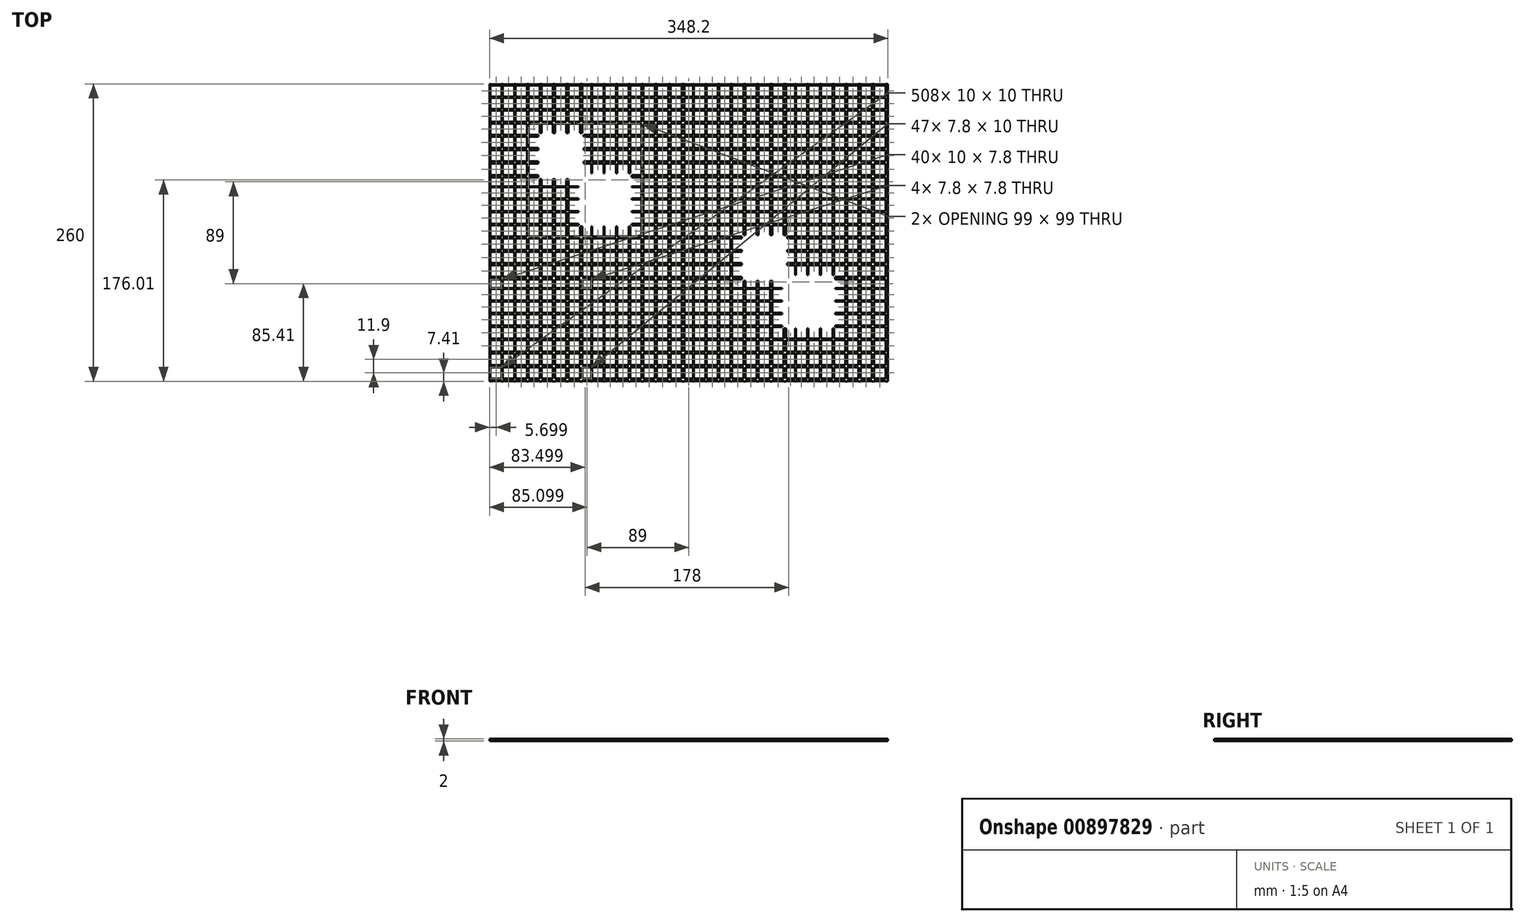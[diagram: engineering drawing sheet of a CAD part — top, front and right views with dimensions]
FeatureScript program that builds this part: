
annotation { "Feature Type Name" : "Feature", "Feature Type Description" : "" }
export const myFeature = defineFeature(function(context is Context, id is Id, definition is map)
    precondition{}
    {
        {
            var Q0;
            Q0=qCreatedBy(makeId("Top.planeOp"),FACE);
            var sketch = newSketch(context, id + "F0", { "sketchPlane" : qUnion([Q0])});
            skLineSegment(sketch, "E0.bottom", {"start": v(-169.44, 136.35) * mm, "end": v(-168.74, 136.35) * mm});
            skLineSegment(sketch, "E0.top", {"start": v(-169.44, -123.65) * mm, "end": v(-168.74, -123.65) * mm});
            skLineSegment(sketch, "E0.left", {"start": v(-169.44, 136.35) * mm, "end": v(-169.44, -123.65) * mm});
            skLineSegment(sketch, "E0.right", {"start": v(-168.74, 136.35) * mm, "end": v(-168.74, -123.65) * mm});
            skLineSegment(sketch, "E1.bottom", {"start": v(-158.74, 136.35) * mm, "end": v(-157.84, 136.35) * mm});
            skLineSegment(sketch, "E1.top", {"start": v(-158.74, -123.65) * mm, "end": v(-157.84, -123.65) * mm});
            skLineSegment(sketch, "E1.left", {"start": v(-158.74, 136.35) * mm, "end": v(-158.74, -123.65) * mm});
            skLineSegment(sketch, "E1.right", {"start": v(-157.84, 136.35) * mm, "end": v(-157.84, -123.65) * mm});
            skLineSegment(sketch, "E2.bottom", {"start": v(-147.84, 136.35) * mm, "end": v(-146.74, 136.35) * mm});
            skLineSegment(sketch, "E2.top", {"start": v(-147.84, -123.65) * mm, "end": v(-146.74, -123.65) * mm});
            skLineSegment(sketch, "E2.left", {"start": v(-147.84, 136.35) * mm, "end": v(-147.84, -123.65) * mm});
            skLineSegment(sketch, "E2.right", {"start": v(-146.74, 136.35) * mm, "end": v(-146.74, -123.65) * mm});
            skLineSegment(sketch, "E3.bottom", {"start": v(-136.74, 136.35) * mm, "end": v(-135.44, 136.35) * mm});
            skLineSegment(sketch, "E3.top", {"start": v(-136.74, -123.65) * mm, "end": v(-135.44, -123.65) * mm});
            skLineSegment(sketch, "E3.left", {"start": v(-136.74, 136.35) * mm, "end": v(-136.74, -123.65) * mm});
            skLineSegment(sketch, "E3.right", {"start": v(-135.44, 136.35) * mm, "end": v(-135.44, -123.65) * mm});
            skLineSegment(sketch, "E4.bottom", {"start": v(-125.44, 136.35) * mm, "end": v(-123.94, 136.35) * mm});
            skLineSegment(sketch, "E4.top", {"start": v(-125.44, -123.65) * mm, "end": v(-123.94, -123.65) * mm});
            skLineSegment(sketch, "E4.left", {"start": v(-125.44, 136.35) * mm, "end": v(-125.44, -123.65) * mm});
            skLineSegment(sketch, "E4.right", {"start": v(-123.94, 136.35) * mm, "end": v(-123.94, -123.65) * mm});
            skLineSegment(sketch, "E5.bottom", {"start": v(-113.94, 136.35) * mm, "end": v(-112.24, 136.35) * mm});
            skLineSegment(sketch, "E5.top", {"start": v(-113.94, -123.65) * mm, "end": v(-112.24, -123.65) * mm});
            skLineSegment(sketch, "E5.left", {"start": v(-113.94, 136.35) * mm, "end": v(-113.94, -123.65) * mm});
            skLineSegment(sketch, "E5.right", {"start": v(-112.24, 136.35) * mm, "end": v(-112.24, -123.65) * mm});
            skLineSegment(sketch, "E6.bottom", {"start": v(-102.24, 136.35) * mm, "end": v(-100.34, 136.35) * mm});
            skLineSegment(sketch, "E6.top", {"start": v(-102.24, -123.65) * mm, "end": v(-100.34, -123.65) * mm});
            skLineSegment(sketch, "E6.left", {"start": v(-102.24, 136.35) * mm, "end": v(-102.24, -123.65) * mm});
            skLineSegment(sketch, "E6.right", {"start": v(-100.34, 136.35) * mm, "end": v(-100.34, -123.65) * mm});
            skLineSegment(sketch, "E7.bottom", {"start": v(-90.34, 136.35) * mm, "end": v(-88.24, 136.35) * mm});
            skLineSegment(sketch, "E7.top", {"start": v(-90.34, -123.65) * mm, "end": v(-88.24, -123.65) * mm});
            skLineSegment(sketch, "E7.left", {"start": v(-90.34, 136.35) * mm, "end": v(-90.34, -123.65) * mm});
            skLineSegment(sketch, "E7.right", {"start": v(-88.24, 136.35) * mm, "end": v(-88.24, -123.65) * mm});
            skLineSegment(sketch, "E8.1.0.0", {"start": v(-69.74, 136.35) * mm, "end": v(-69.74, -123.65) * mm});
            skLineSegment(sketch, "E8.1.0.1", {"start": v(-13.24, 136.35) * mm, "end": v(-13.24, -123.65) * mm});
            skLineSegment(sketch, "E8.1.0.2", {"start": v(-58.84, 136.35) * mm, "end": v(-58.84, -123.65) * mm});
            skLineSegment(sketch, "E8.1.0.3", {"start": v(-79.74, 136.35) * mm, "end": v(-79.74, -123.65) * mm});
            skLineSegment(sketch, "E8.1.0.4", {"start": v(-68.84, 136.35) * mm, "end": v(-68.84, -123.65) * mm});
            skLineSegment(sketch, "E8.1.0.5", {"start": v(-1.34, 136.35) * mm, "end": v(-1.34, -123.65) * mm});
            skLineSegment(sketch, "E8.1.0.6", {"start": v(-24.94, 136.35) * mm, "end": v(-24.94, -123.65) * mm});
            skLineSegment(sketch, "E8.1.0.7", {"start": v(-36.44, 136.35) * mm, "end": v(-36.44, -123.65) * mm});
            skLineSegment(sketch, "E8.1.0.8", {"start": v(-80.44, 136.35) * mm, "end": v(-80.44, -123.65) * mm});
            skLineSegment(sketch, "E8.1.0.9", {"start": v(-47.74, 136.35) * mm, "end": v(-47.74, -123.65) * mm});
            skLineSegment(sketch, "E8.1.0.10", {"start": v(-11.34, 136.35) * mm, "end": v(-11.34, -123.65) * mm});
            skLineSegment(sketch, "E8.1.0.11", {"start": v(-34.94, 136.35) * mm, "end": v(-34.94, -123.65) * mm});
            skLineSegment(sketch, "E8.1.0.12", {"start": v(0.76, 136.35) * mm, "end": v(0.76, -123.65) * mm});
            skLineSegment(sketch, "E8.1.0.13", {"start": v(-23.24, 136.35) * mm, "end": v(-23.24, -123.65) * mm});
            skLineSegment(sketch, "E8.1.0.14", {"start": v(-57.74, 136.35) * mm, "end": v(-57.74, -123.65) * mm});
            skLineSegment(sketch, "E8.1.0.15", {"start": v(-46.44, 136.35) * mm, "end": v(-46.44, -123.65) * mm});
            skLineSegment(sketch, "E8.1.0.16", {"start": v(-69.74, -123.65) * mm, "end": v(-68.84, -123.65) * mm});
            skLineSegment(sketch, "E8.1.0.17", {"start": v(-58.84, 136.35) * mm, "end": v(-57.74, 136.35) * mm});
            skLineSegment(sketch, "E8.1.0.18", {"start": v(-13.24, -123.65) * mm, "end": v(-11.34, -123.65) * mm});
            skLineSegment(sketch, "E8.1.0.19", {"start": v(-36.44, -123.65) * mm, "end": v(-34.94, -123.65) * mm});
            skLineSegment(sketch, "E8.1.0.20", {"start": v(-1.34, 136.35) * mm, "end": v(0.76, 136.35) * mm});
            skLineSegment(sketch, "E8.1.0.21", {"start": v(-69.74, 136.35) * mm, "end": v(-68.84, 136.35) * mm});
            skLineSegment(sketch, "E8.1.0.22", {"start": v(-80.44, -123.65) * mm, "end": v(-79.74, -123.65) * mm});
            skLineSegment(sketch, "E8.1.0.23", {"start": v(-36.44, 136.35) * mm, "end": v(-34.94, 136.35) * mm});
            skLineSegment(sketch, "E8.1.0.24", {"start": v(-80.44, 136.35) * mm, "end": v(-79.74, 136.35) * mm});
            skLineSegment(sketch, "E8.1.0.25", {"start": v(-24.94, 136.35) * mm, "end": v(-23.24, 136.35) * mm});
            skLineSegment(sketch, "E8.1.0.26", {"start": v(-58.84, -123.65) * mm, "end": v(-57.74, -123.65) * mm});
            skLineSegment(sketch, "E8.1.0.27", {"start": v(-1.34, -123.65) * mm, "end": v(0.76, -123.65) * mm});
            skLineSegment(sketch, "E8.1.0.28", {"start": v(-13.24, 136.35) * mm, "end": v(-11.34, 136.35) * mm});
            skLineSegment(sketch, "E8.1.0.29", {"start": v(-24.94, -123.65) * mm, "end": v(-23.24, -123.65) * mm});
            skLineSegment(sketch, "E8.1.0.30", {"start": v(-47.74, 136.35) * mm, "end": v(-46.44, 136.35) * mm});
            skLineSegment(sketch, "E8.1.0.31", {"start": v(-47.74, -123.65) * mm, "end": v(-46.44, -123.65) * mm});
            skLineSegment(sketch, "E8.2.0.0", {"start": v(19.26, 136.35) * mm, "end": v(19.26, -123.65) * mm});
            skLineSegment(sketch, "E8.2.0.1", {"start": v(75.76, 136.35) * mm, "end": v(75.76, -123.65) * mm});
            skLineSegment(sketch, "E8.2.0.2", {"start": v(30.16, 136.35) * mm, "end": v(30.16, -123.65) * mm});
            skLineSegment(sketch, "E8.2.0.3", {"start": v(9.26, 136.35) * mm, "end": v(9.26, -123.65) * mm});
            skLineSegment(sketch, "E8.2.0.4", {"start": v(20.16, 136.35) * mm, "end": v(20.16, -123.65) * mm});
            skLineSegment(sketch, "E8.2.0.5", {"start": v(87.66, 136.35) * mm, "end": v(87.66, -123.65) * mm});
            skLineSegment(sketch, "E8.2.0.6", {"start": v(64.06, 136.35) * mm, "end": v(64.06, -123.65) * mm});
            skLineSegment(sketch, "E8.2.0.7", {"start": v(52.56, 136.35) * mm, "end": v(52.56, -123.65) * mm});
            skLineSegment(sketch, "E8.2.0.8", {"start": v(8.56, 136.35) * mm, "end": v(8.56, -123.65) * mm});
            skLineSegment(sketch, "E8.2.0.9", {"start": v(41.26, 136.35) * mm, "end": v(41.26, -123.65) * mm});
            skLineSegment(sketch, "E8.2.0.10", {"start": v(77.66, 136.35) * mm, "end": v(77.66, -123.65) * mm});
            skLineSegment(sketch, "E8.2.0.11", {"start": v(54.06, 136.35) * mm, "end": v(54.06, -123.65) * mm});
            skLineSegment(sketch, "E8.2.0.12", {"start": v(89.76, 136.35) * mm, "end": v(89.76, -123.65) * mm});
            skLineSegment(sketch, "E8.2.0.13", {"start": v(65.76, 136.35) * mm, "end": v(65.76, -123.65) * mm});
            skLineSegment(sketch, "E8.2.0.14", {"start": v(31.26, 136.35) * mm, "end": v(31.26, -123.65) * mm});
            skLineSegment(sketch, "E8.2.0.15", {"start": v(42.56, 136.35) * mm, "end": v(42.56, -123.65) * mm});
            skLineSegment(sketch, "E8.2.0.16", {"start": v(19.26, -123.65) * mm, "end": v(20.16, -123.65) * mm});
            skLineSegment(sketch, "E8.2.0.17", {"start": v(30.16, 136.35) * mm, "end": v(31.26, 136.35) * mm});
            skLineSegment(sketch, "E8.2.0.18", {"start": v(75.76, -123.65) * mm, "end": v(77.66, -123.65) * mm});
            skLineSegment(sketch, "E8.2.0.19", {"start": v(52.56, -123.65) * mm, "end": v(54.06, -123.65) * mm});
            skLineSegment(sketch, "E8.2.0.20", {"start": v(87.66, 136.35) * mm, "end": v(89.76, 136.35) * mm});
            skLineSegment(sketch, "E8.2.0.21", {"start": v(19.26, 136.35) * mm, "end": v(20.16, 136.35) * mm});
            skLineSegment(sketch, "E8.2.0.22", {"start": v(8.56, -123.65) * mm, "end": v(9.26, -123.65) * mm});
            skLineSegment(sketch, "E8.2.0.23", {"start": v(52.56, 136.35) * mm, "end": v(54.06, 136.35) * mm});
            skLineSegment(sketch, "E8.2.0.24", {"start": v(8.56, 136.35) * mm, "end": v(9.26, 136.35) * mm});
            skLineSegment(sketch, "E8.2.0.25", {"start": v(64.06, 136.35) * mm, "end": v(65.76, 136.35) * mm});
            skLineSegment(sketch, "E8.2.0.26", {"start": v(30.16, -123.65) * mm, "end": v(31.26, -123.65) * mm});
            skLineSegment(sketch, "E8.2.0.27", {"start": v(87.66, -123.65) * mm, "end": v(89.76, -123.65) * mm});
            skLineSegment(sketch, "E8.2.0.28", {"start": v(75.76, 136.35) * mm, "end": v(77.66, 136.35) * mm});
            skLineSegment(sketch, "E8.2.0.29", {"start": v(64.06, -123.65) * mm, "end": v(65.76, -123.65) * mm});
            skLineSegment(sketch, "E8.2.0.30", {"start": v(41.26, 136.35) * mm, "end": v(42.56, 136.35) * mm});
            skLineSegment(sketch, "E8.2.0.31", {"start": v(41.26, -123.65) * mm, "end": v(42.56, -123.65) * mm});
            skLineSegment(sketch, "E8.direction1", {"start": v(-169.44, -123.65) * mm, "end": v(-80.44, -123.65) * mm, "construction": true});
            skLineSegment(sketch, "E9.0.3.0", {"start": v(108.26, 136.35) * mm, "end": v(108.26, -123.65) * mm});
            skLineSegment(sketch, "E9.3.3.0", {"start": v(164.76, 136.35) * mm, "end": v(164.76, -123.65) * mm});
            skLineSegment(sketch, "E9.6.3.0", {"start": v(119.16, 136.35) * mm, "end": v(119.16, -123.65) * mm});
            skLineSegment(sketch, "E9.9.3.0", {"start": v(98.26, 136.35) * mm, "end": v(98.26, -123.65) * mm});
            skLineSegment(sketch, "E9.12.3.0", {"start": v(109.16, 136.35) * mm, "end": v(109.16, -123.65) * mm});
            skLineSegment(sketch, "E9.15.3.0", {"start": v(176.66, 136.35) * mm, "end": v(176.66, -123.65) * mm});
            skLineSegment(sketch, "E9.18.3.0", {"start": v(153.06, 136.35) * mm, "end": v(153.06, -123.65) * mm});
            skLineSegment(sketch, "E9.21.3.0", {"start": v(141.56, 136.35) * mm, "end": v(141.56, -123.65) * mm});
            skLineSegment(sketch, "E9.24.3.0", {"start": v(97.56, 136.35) * mm, "end": v(97.56, -123.65) * mm});
            skLineSegment(sketch, "E9.27.3.0", {"start": v(130.26, 136.35) * mm, "end": v(130.26, -123.65) * mm});
            skLineSegment(sketch, "E9.30.3.0", {"start": v(166.66, 136.35) * mm, "end": v(166.66, -123.65) * mm});
            skLineSegment(sketch, "E9.33.3.0", {"start": v(143.06, 136.35) * mm, "end": v(143.06, -123.65) * mm});
            skLineSegment(sketch, "E9.36.3.0", {"start": v(178.76, 136.35) * mm, "end": v(178.76, -123.65) * mm});
            skLineSegment(sketch, "E9.39.3.0", {"start": v(154.76, 136.35) * mm, "end": v(154.76, -123.65) * mm});
            skLineSegment(sketch, "E9.42.3.0", {"start": v(120.26, 136.35) * mm, "end": v(120.26, -123.65) * mm});
            skLineSegment(sketch, "E9.45.3.0", {"start": v(131.56, 136.35) * mm, "end": v(131.56, -123.65) * mm});
            skLineSegment(sketch, "E9.48.3.0", {"start": v(108.26, -123.65) * mm, "end": v(109.16, -123.65) * mm});
            skLineSegment(sketch, "E9.51.3.0", {"start": v(119.16, 136.35) * mm, "end": v(120.26, 136.35) * mm});
            skLineSegment(sketch, "E9.54.3.0", {"start": v(164.76, -123.65) * mm, "end": v(166.66, -123.65) * mm});
            skLineSegment(sketch, "E9.57.3.0", {"start": v(141.56, -123.65) * mm, "end": v(143.06, -123.65) * mm});
            skLineSegment(sketch, "E9.60.3.0", {"start": v(176.66, 136.35) * mm, "end": v(178.76, 136.35) * mm});
            skLineSegment(sketch, "E9.63.3.0", {"start": v(108.26, 136.35) * mm, "end": v(109.16, 136.35) * mm});
            skLineSegment(sketch, "E9.66.3.0", {"start": v(97.56, -123.65) * mm, "end": v(98.26, -123.65) * mm});
            skLineSegment(sketch, "E9.69.3.0", {"start": v(141.56, 136.35) * mm, "end": v(143.06, 136.35) * mm});
            skLineSegment(sketch, "E9.72.3.0", {"start": v(97.56, 136.35) * mm, "end": v(98.26, 136.35) * mm});
            skLineSegment(sketch, "E9.75.3.0", {"start": v(153.06, 136.35) * mm, "end": v(154.76, 136.35) * mm});
            skLineSegment(sketch, "E9.78.3.0", {"start": v(119.16, -123.65) * mm, "end": v(120.26, -123.65) * mm});
            skLineSegment(sketch, "E9.81.3.0", {"start": v(176.66, -123.65) * mm, "end": v(178.76, -123.65) * mm});
            skLineSegment(sketch, "E9.84.3.0", {"start": v(164.76, 136.35) * mm, "end": v(166.66, 136.35) * mm});
            skLineSegment(sketch, "E9.87.3.0", {"start": v(153.06, -123.65) * mm, "end": v(154.76, -123.65) * mm});
            skLineSegment(sketch, "E9.90.3.0", {"start": v(130.26, 136.35) * mm, "end": v(131.56, 136.35) * mm});
            skLineSegment(sketch, "E9.93.3.0", {"start": v(130.26, -123.65) * mm, "end": v(131.56, -123.65) * mm});
            skSolve(sketch);
        }
        {
            var Q0;
            Q0 = qSketchRegion(id + "F0", true);
            extrude(context, id + "F1", {"entities" : qUnion([Q0]), "depth" : 2 * mm, "offsetDistance" : 25 * mm});
        }
        {
            var Q0;
            Q0=qCreatedBy(makeId("Top.planeOp"),FACE);
            var sketch = newSketch(context, id + "F2", { "sketchPlane" : qUnion([Q0])});
            skLineSegment(sketch, "E10.bottom", {"start": v(178.3, 135.86) * mm, "end": v(178.3, 135.16) * mm});
            skLineSegment(sketch, "E10.top", {"start": v(-169.1, 135.86) * mm, "end": v(-169.1, 135.16) * mm});
            skLineSegment(sketch, "E10.left", {"start": v(178.3, 135.86) * mm, "end": v(-169.1, 135.86) * mm});
            skLineSegment(sketch, "E10.right", {"start": v(178.3, 135.16) * mm, "end": v(-169.1, 135.16) * mm});
            skLineSegment(sketch, "E11.bottom", {"start": v(178.3, 125.16) * mm, "end": v(178.3, 124.26) * mm});
            skLineSegment(sketch, "E11.top", {"start": v(-169.1, 125.16) * mm, "end": v(-169.1, 124.26) * mm});
            skLineSegment(sketch, "E11.left", {"start": v(178.3, 125.16) * mm, "end": v(-169.1, 125.16) * mm});
            skLineSegment(sketch, "E11.right", {"start": v(178.3, 124.26) * mm, "end": v(-169.1, 124.26) * mm});
            skLineSegment(sketch, "E12.bottom", {"start": v(178.3, 114.26) * mm, "end": v(178.3, 113.16) * mm});
            skLineSegment(sketch, "E12.top", {"start": v(-169.1, 114.26) * mm, "end": v(-169.1, 113.16) * mm});
            skLineSegment(sketch, "E12.left", {"start": v(178.3, 114.26) * mm, "end": v(-169.1, 114.26) * mm});
            skLineSegment(sketch, "E12.right", {"start": v(178.3, 113.16) * mm, "end": v(-169.1, 113.16) * mm});
            skLineSegment(sketch, "E13.bottom", {"start": v(178.3, 103.16) * mm, "end": v(178.3, 101.86) * mm});
            skLineSegment(sketch, "E13.top", {"start": v(-169.1, 103.16) * mm, "end": v(-169.1, 101.86) * mm});
            skLineSegment(sketch, "E13.left", {"start": v(178.3, 103.16) * mm, "end": v(-169.1, 103.16) * mm});
            skLineSegment(sketch, "E13.right", {"start": v(178.3, 101.86) * mm, "end": v(-169.1, 101.86) * mm});
            skLineSegment(sketch, "E14.bottom", {"start": v(178.3, 91.86) * mm, "end": v(178.3, 90.36) * mm});
            skLineSegment(sketch, "E14.top", {"start": v(-169.1, 91.86) * mm, "end": v(-169.1, 90.36) * mm});
            skLineSegment(sketch, "E14.left", {"start": v(178.3, 91.86) * mm, "end": v(-169.1, 91.86) * mm});
            skLineSegment(sketch, "E14.right", {"start": v(178.3, 90.36) * mm, "end": v(-169.1, 90.36) * mm});
            skLineSegment(sketch, "E15.bottom", {"start": v(178.3, 80.36) * mm, "end": v(178.3, 78.66) * mm});
            skLineSegment(sketch, "E15.top", {"start": v(-169.1, 80.36) * mm, "end": v(-169.1, 78.66) * mm});
            skLineSegment(sketch, "E15.left", {"start": v(178.3, 80.36) * mm, "end": v(-169.1, 80.36) * mm});
            skLineSegment(sketch, "E15.right", {"start": v(178.3, 78.66) * mm, "end": v(-169.1, 78.66) * mm});
            skLineSegment(sketch, "E16.bottom", {"start": v(178.3, 68.66) * mm, "end": v(178.3, 66.76) * mm});
            skLineSegment(sketch, "E16.top", {"start": v(-169.1, 68.66) * mm, "end": v(-169.1, 66.76) * mm});
            skLineSegment(sketch, "E16.left", {"start": v(178.3, 68.66) * mm, "end": v(-169.1, 68.66) * mm});
            skLineSegment(sketch, "E16.right", {"start": v(178.3, 66.76) * mm, "end": v(-169.1, 66.76) * mm});
            skLineSegment(sketch, "E17.bottom", {"start": v(178.3, 56.76) * mm, "end": v(178.3, 54.66) * mm});
            skLineSegment(sketch, "E17.top", {"start": v(-169.1, 56.76) * mm, "end": v(-169.1, 54.66) * mm});
            skLineSegment(sketch, "E17.left", {"start": v(178.3, 56.76) * mm, "end": v(-169.1, 56.76) * mm});
            skLineSegment(sketch, "E17.right", {"start": v(178.3, 54.66) * mm, "end": v(-169.1, 54.66) * mm});
            skLineSegment(sketch, "E18.1.0.0", {"start": v(178.3, 36.16) * mm, "end": v(-169.1, 36.16) * mm});
            skLineSegment(sketch, "E18.1.0.1", {"start": v(178.3, -20.34) * mm, "end": v(-169.1, -20.34) * mm});
            skLineSegment(sketch, "E18.1.0.2", {"start": v(178.3, 25.26) * mm, "end": v(-169.1, 25.26) * mm});
            skLineSegment(sketch, "E18.1.0.3", {"start": v(178.3, 46.16) * mm, "end": v(-169.1, 46.16) * mm});
            skLineSegment(sketch, "E18.1.0.4", {"start": v(178.3, 35.26) * mm, "end": v(-169.1, 35.26) * mm});
            skLineSegment(sketch, "E18.1.0.5", {"start": v(178.3, -32.24) * mm, "end": v(-169.1, -32.24) * mm});
            skLineSegment(sketch, "E18.1.0.6", {"start": v(178.3, -8.64) * mm, "end": v(-169.1, -8.64) * mm});
            skLineSegment(sketch, "E18.1.0.7", {"start": v(178.3, 2.86) * mm, "end": v(-169.1, 2.86) * mm});
            skLineSegment(sketch, "E18.1.0.8", {"start": v(178.3, 46.86) * mm, "end": v(-169.1, 46.86) * mm});
            skLineSegment(sketch, "E18.1.0.9", {"start": v(178.3, 14.16) * mm, "end": v(-169.1, 14.16) * mm});
            skLineSegment(sketch, "E18.1.0.10", {"start": v(178.3, -22.24) * mm, "end": v(-169.1, -22.24) * mm});
            skLineSegment(sketch, "E18.1.0.11", {"start": v(178.3, 1.36) * mm, "end": v(-169.1, 1.36) * mm});
            skLineSegment(sketch, "E18.1.0.12", {"start": v(178.3, -34.34) * mm, "end": v(-169.1, -34.34) * mm});
            skLineSegment(sketch, "E18.1.0.13", {"start": v(178.3, -10.34) * mm, "end": v(-169.1, -10.34) * mm});
            skLineSegment(sketch, "E18.1.0.14", {"start": v(178.3, 24.16) * mm, "end": v(-169.1, 24.16) * mm});
            skLineSegment(sketch, "E18.1.0.15", {"start": v(178.3, 12.86) * mm, "end": v(-169.1, 12.86) * mm});
            skLineSegment(sketch, "E18.1.0.16", {"start": v(-169.1, 36.16) * mm, "end": v(-169.1, 35.26) * mm});
            skLineSegment(sketch, "E18.1.0.17", {"start": v(178.3, 25.26) * mm, "end": v(178.3, 24.16) * mm});
            skLineSegment(sketch, "E18.1.0.18", {"start": v(-169.1, -20.34) * mm, "end": v(-169.1, -22.24) * mm});
            skLineSegment(sketch, "E18.1.0.19", {"start": v(-169.1, 2.86) * mm, "end": v(-169.1, 1.36) * mm});
            skLineSegment(sketch, "E18.1.0.20", {"start": v(178.3, -32.24) * mm, "end": v(178.3, -34.34) * mm});
            skLineSegment(sketch, "E18.1.0.21", {"start": v(178.3, 36.16) * mm, "end": v(178.3, 35.26) * mm});
            skLineSegment(sketch, "E18.1.0.22", {"start": v(-169.1, 46.86) * mm, "end": v(-169.1, 46.16) * mm});
            skLineSegment(sketch, "E18.1.0.23", {"start": v(178.3, 2.86) * mm, "end": v(178.3, 1.36) * mm});
            skLineSegment(sketch, "E18.1.0.24", {"start": v(178.3, 46.86) * mm, "end": v(178.3, 46.16) * mm});
            skLineSegment(sketch, "E18.1.0.25", {"start": v(178.3, -8.64) * mm, "end": v(178.3, -10.34) * mm});
            skLineSegment(sketch, "E18.1.0.26", {"start": v(-169.1, 25.26) * mm, "end": v(-169.1, 24.16) * mm});
            skLineSegment(sketch, "E18.1.0.27", {"start": v(-169.1, -32.24) * mm, "end": v(-169.1, -34.34) * mm});
            skLineSegment(sketch, "E18.1.0.28", {"start": v(178.3, -20.34) * mm, "end": v(178.3, -22.24) * mm});
            skLineSegment(sketch, "E18.1.0.29", {"start": v(-169.1, -8.64) * mm, "end": v(-169.1, -10.34) * mm});
            skLineSegment(sketch, "E18.1.0.30", {"start": v(178.3, 14.16) * mm, "end": v(178.3, 12.86) * mm});
            skLineSegment(sketch, "E18.1.0.31", {"start": v(-169.1, 14.16) * mm, "end": v(-169.1, 12.86) * mm});
            skLineSegment(sketch, "E18.2.0.0", {"start": v(178.3, -52.84) * mm, "end": v(-169.1, -52.84) * mm});
            skLineSegment(sketch, "E18.2.0.1", {"start": v(178.3, -109.34) * mm, "end": v(-169.1, -109.34) * mm});
            skLineSegment(sketch, "E18.2.0.2", {"start": v(178.3, -63.74) * mm, "end": v(-169.1, -63.74) * mm});
            skLineSegment(sketch, "E18.2.0.3", {"start": v(178.3, -42.84) * mm, "end": v(-169.1, -42.84) * mm});
            skLineSegment(sketch, "E18.2.0.4", {"start": v(178.3, -53.74) * mm, "end": v(-169.1, -53.74) * mm});
            skLineSegment(sketch, "E18.2.0.5", {"start": v(178.3, -121.24) * mm, "end": v(-169.1, -121.24) * mm});
            skLineSegment(sketch, "E18.2.0.6", {"start": v(178.3, -97.64) * mm, "end": v(-169.1, -97.64) * mm});
            skLineSegment(sketch, "E18.2.0.7", {"start": v(178.3, -86.14) * mm, "end": v(-169.1, -86.14) * mm});
            skLineSegment(sketch, "E18.2.0.8", {"start": v(178.3, -42.14) * mm, "end": v(-169.1, -42.14) * mm});
            skLineSegment(sketch, "E18.2.0.9", {"start": v(178.3, -74.84) * mm, "end": v(-169.1, -74.84) * mm});
            skLineSegment(sketch, "E18.2.0.10", {"start": v(178.3, -111.24) * mm, "end": v(-169.1, -111.24) * mm});
            skLineSegment(sketch, "E18.2.0.11", {"start": v(178.3, -87.64) * mm, "end": v(-169.1, -87.64) * mm});
            skLineSegment(sketch, "E18.2.0.12", {"start": v(178.3, -123.34) * mm, "end": v(-169.1, -123.34) * mm});
            skLineSegment(sketch, "E18.2.0.13", {"start": v(178.3, -99.34) * mm, "end": v(-169.1, -99.34) * mm});
            skLineSegment(sketch, "E18.2.0.14", {"start": v(178.3, -64.84) * mm, "end": v(-169.1, -64.84) * mm});
            skLineSegment(sketch, "E18.2.0.15", {"start": v(178.3, -76.14) * mm, "end": v(-169.1, -76.14) * mm});
            skLineSegment(sketch, "E18.2.0.16", {"start": v(-169.1, -52.84) * mm, "end": v(-169.1, -53.74) * mm});
            skLineSegment(sketch, "E18.2.0.17", {"start": v(178.3, -63.74) * mm, "end": v(178.3, -64.84) * mm});
            skLineSegment(sketch, "E18.2.0.18", {"start": v(-169.1, -109.34) * mm, "end": v(-169.1, -111.24) * mm});
            skLineSegment(sketch, "E18.2.0.19", {"start": v(-169.1, -86.14) * mm, "end": v(-169.1, -87.64) * mm});
            skLineSegment(sketch, "E18.2.0.20", {"start": v(178.3, -121.24) * mm, "end": v(178.3, -123.34) * mm});
            skLineSegment(sketch, "E18.2.0.21", {"start": v(178.3, -52.84) * mm, "end": v(178.3, -53.74) * mm});
            skLineSegment(sketch, "E18.2.0.22", {"start": v(-169.1, -42.14) * mm, "end": v(-169.1, -42.84) * mm});
            skLineSegment(sketch, "E18.2.0.23", {"start": v(178.3, -86.14) * mm, "end": v(178.3, -87.64) * mm});
            skLineSegment(sketch, "E18.2.0.24", {"start": v(178.3, -42.14) * mm, "end": v(178.3, -42.84) * mm});
            skLineSegment(sketch, "E18.2.0.25", {"start": v(178.3, -97.64) * mm, "end": v(178.3, -99.34) * mm});
            skLineSegment(sketch, "E18.2.0.26", {"start": v(-169.1, -63.74) * mm, "end": v(-169.1, -64.84) * mm});
            skLineSegment(sketch, "E18.2.0.27", {"start": v(-169.1, -121.24) * mm, "end": v(-169.1, -123.34) * mm});
            skLineSegment(sketch, "E18.2.0.28", {"start": v(178.3, -109.34) * mm, "end": v(178.3, -111.24) * mm});
            skLineSegment(sketch, "E18.2.0.29", {"start": v(-169.1, -97.64) * mm, "end": v(-169.1, -99.34) * mm});
            skLineSegment(sketch, "E18.2.0.30", {"start": v(178.3, -74.84) * mm, "end": v(178.3, -76.14) * mm});
            skLineSegment(sketch, "E18.2.0.31", {"start": v(-169.1, -74.84) * mm, "end": v(-169.1, -76.14) * mm});
            skLineSegment(sketch, "E18.direction1", {"start": v(-169.1, 135.86) * mm, "end": v(-169.1, 46.86) * mm, "construction": true});
            skSolve(sketch);
        }
        {
            var Q0;
            Q0 = qSketchRegion(id + "F2", true);
            extrude(context, id + "F3", {"entities" : qUnion([Q0]), "operationType" : NewBodyOperationType.ADD, "depth" : 2 * mm, "offsetDistance" : 25 * mm});
        }
        {
            var Q0;
            Q0=qCreatedBy(makeId("Top.planeOp"),FACE);
            var sketch = newSketch(context, id + "F4", { "sketchPlane" : qUnion([Q0])});
            skLineSegment(sketch, "E19.bottom", {"start": v(-126.65, 93.35) * mm, "end": v(-87.04, 93.35) * mm});
            skLineSegment(sketch, "E19.top", {"start": v(-126.65, 53.1) * mm, "end": v(-91.59, 53.1) * mm});
            skLineSegment(sketch, "E19.left", {"start": v(-126.65, 93.35) * mm, "end": v(-126.65, 53.1) * mm});
            skLineSegment(sketch, "E19.right", {"start": v(-87.04, 93.35) * mm, "end": v(-87.04, 58.29) * mm});
            skLineSegment(sketch, "E20.bottom", {"start": v(-87.04, 58.29) * mm, "end": v(-45.23, 58.29) * mm});
            skLineSegment(sketch, "E20.top", {"start": v(-91.59, 11.74) * mm, "end": v(-45.23, 11.74) * mm});
            skLineSegment(sketch, "E20.left", {"start": v(-91.59, 53.1) * mm, "end": v(-91.59, 11.74) * mm});
            skLineSegment(sketch, "E20.right", {"start": v(-45.23, 58.29) * mm, "end": v(-45.23, 11.74) * mm});
            skLineSegment(sketch, "E21.bottom", {"start": v(51.14, 4.4) * mm, "end": v(90.75, 4.4) * mm});
            skLineSegment(sketch, "E21.top", {"start": v(51.14, -35.85) * mm, "end": v(86.2, -35.85) * mm});
            skLineSegment(sketch, "E21.left", {"start": v(51.14, 4.4) * mm, "end": v(51.14, -35.85) * mm});
            skLineSegment(sketch, "E21.right", {"start": v(90.75, 4.4) * mm, "end": v(90.75, -30.66) * mm});
            skLineSegment(sketch, "E22.bottom", {"start": v(90.75, -30.66) * mm, "end": v(132.56, -30.66) * mm});
            skLineSegment(sketch, "E22.top", {"start": v(86.2, -77.2) * mm, "end": v(132.56, -77.2) * mm});
            skLineSegment(sketch, "E22.left", {"start": v(86.2, -35.85) * mm, "end": v(86.2, -77.2) * mm});
            skLineSegment(sketch, "E22.right", {"start": v(132.56, -30.66) * mm, "end": v(132.56, -77.2) * mm});
            skSolve(sketch);
        }
        {
            var Q0;
            Q0 = qSketchRegion(id + "F4", true);
            extrude(context, id + "F5", {"entities" : qUnion([Q0]), "operationType" : NewBodyOperationType.REMOVE, "depth" : 25 * mm, "offsetDistance" : 25 * mm});
        }
    });
